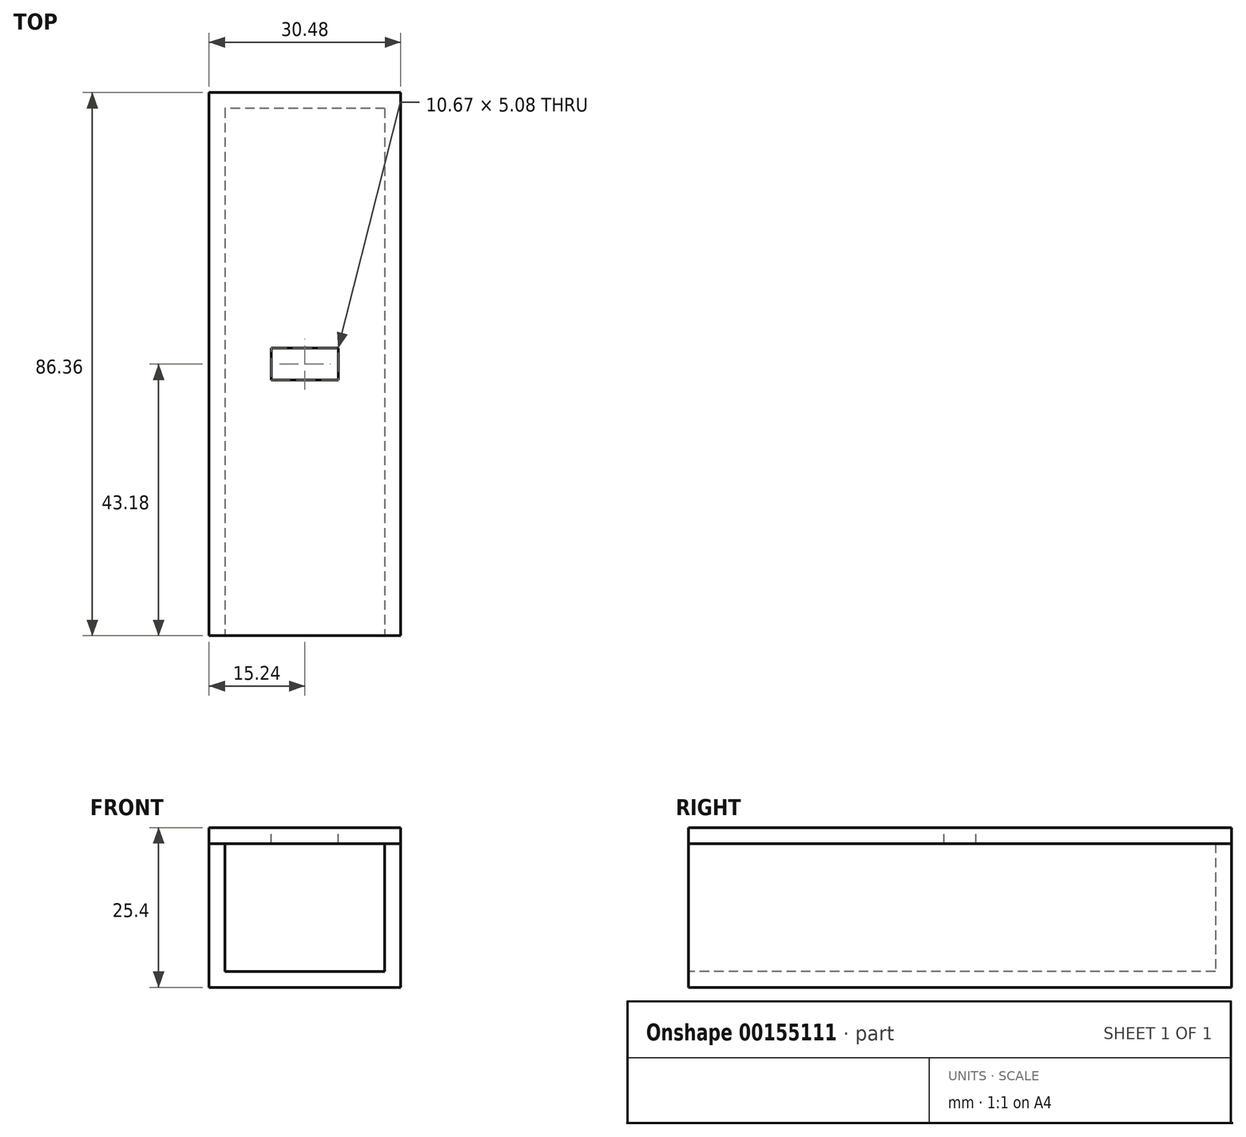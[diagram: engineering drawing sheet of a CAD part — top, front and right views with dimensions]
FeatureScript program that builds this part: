
annotation { "Feature Type Name" : "Feature", "Feature Type Description" : "" }
export const myFeature = defineFeature(function(context is Context, id is Id, definition is map)
    precondition{}
    {
        {
            var Q0;
            Q0=qCreatedBy(makeId("Top.planeOp"),FACE);
            var sketch = newSketch(context, id + "F0", { "sketchPlane" : qUnion([Q0])});
            skLineSegment(sketch, "E0.bottom", {"start": v(12.7, 40.64) * mm, "end": v(-12.7, 40.64) * mm});
            skLineSegment(sketch, "E0.top", {"start": v(12.7, -40.64) * mm, "end": v(-12.7, -40.64) * mm});
            skLineSegment(sketch, "E0.left", {"start": v(12.7, 40.64) * mm, "end": v(12.7, -40.64) * mm});
            skLineSegment(sketch, "E0.right", {"start": v(-12.7, 40.64) * mm, "end": v(-12.7, -40.64) * mm});
            skPoint(sketch, "E0.middle", {"position": v(0, 0) * mm});
            skLineSegment(sketch, "E1.bottom", {"start": v(15.24, 43.18) * mm, "end": v(-15.24, 43.18) * mm});
            skLineSegment(sketch, "E1.top", {"start": v(15.24, -43.18) * mm, "end": v(-15.24, -43.18) * mm});
            skLineSegment(sketch, "E1.left", {"start": v(15.24, 43.18) * mm, "end": v(15.24, -43.18) * mm});
            skLineSegment(sketch, "E1.right", {"start": v(-15.24, 43.18) * mm, "end": v(-15.24, -43.18) * mm});
            skLineSegment(sketch, "E2", {"start": v(-12.7, -40.64) * mm, "end": v(-12.7, -43.18) * mm});
            skLineSegment(sketch, "E3", {"start": v(-12.7, -43.18) * mm, "end": v(12.7, -43.18) * mm});
            skLineSegment(sketch, "E4", {"start": v(12.7, -43.18) * mm, "end": v(12.7, -40.64) * mm});
            skSolve(sketch);
        }
        {
            var Q0;
            Q0 = qSketchRegion(id + "F0", true);
            var Q1;
            Q1=makeQuery(id+"F0.imprint","IMPRINT",FACE,{"disambiguationData":[TD([[makeQuery(id+"F0.imprint","IMPRINT",EDGE,{"derivedFrom":sQuery(id+"F0.wireOp",EDGE,"E0.bottom")}),1.0]])]});
            extrude(context, id + "F1", {"entities" : qUnion([Q0, Q1]), "oppositeDirection" : true, "depth" : 2.54 * mm});
        }
        {
            var Q0;
            Q0=makeQuery(id+"F0.imprint","IMPRINT",FACE,{"disambiguationData":[TD([[makeQuery(id+"F0.imprint","IMPRINT",EDGE,{"derivedFrom":sQuery(id+"F0.wireOp",EDGE,"E0.bottom")}),-1.0]])]});
            extrude(context, id + "F2", {"entities" : qUnion([Q0]), "operationType" : NewBodyOperationType.ADD, "depth" : 20.32 * mm});
        }
        {
            var Q0;
            Q0=makeQuery(id+"F0.imprint","IMPRINT",FACE,{"disambiguationData":[TD([[makeQuery(id+"F0.imprint","IMPRINT",EDGE,{"derivedFrom":sQuery(id+"F0.wireOp",EDGE,"E0.bottom")}),1.0]])]});
            var Q1;
            Q1=makeQuery(id+"F0.imprint","IMPRINT",FACE,{"disambiguationData":[TD([[makeQuery(id+"F0.imprint","IMPRINT",EDGE,{"derivedFrom":sQuery(id+"F0.wireOp",EDGE,"E0.bottom")}),-1.0]])]});
            var Q2;
            Q2=makeQuery(id+"F0.imprint","IMPRINT",FACE,{"disambiguationData":[TD([[makeQuery(id+"F0.imprint","IMPRINT",EDGE,{"derivedFrom":sQuery(id+"F0.wireOp",EDGE,"E0.top")}),1.0]])]});
            extrude(context, id + "F3", {"entities" : qUnion([Q0, Q1, Q2]), "depth" : 22.86 * mm, "hasSecondDirection" : true, "secondDirectionOppositeDirection" : false, "secondDirectionDepth" : 20.32 * mm});
        }
        {
            var Q0;
            Q0=makeQuery(id+"F3.opExtrude","CAP_FACE",FACE,{"disambiguationData":[OSD([sQuery(id+"F0.wireOp",EDGE,"E1.bottom"),sQuery(id+"F0.wireOp",EDGE,"E1.top"),sQuery(id+"F0.wireOp",EDGE,"E1.left"),sQuery(id+"F0.wireOp",EDGE,"E1.right"),sQuery(id+"F0.wireOp",EDGE,"E3")])],"isStart":false});
            var sketch = newSketch(context, id + "F4", { "sketchPlane" : qUnion([Q0])});
            skLineSegment(sketch, "E5.bottom", {"start": v(5.33, 2.54) * mm, "end": v(-5.33, 2.54) * mm});
            skLineSegment(sketch, "E5.top", {"start": v(5.33, -2.54) * mm, "end": v(-5.33, -2.54) * mm});
            skLineSegment(sketch, "E5.left", {"start": v(5.33, 2.54) * mm, "end": v(5.33, -2.54) * mm});
            skLineSegment(sketch, "E5.right", {"start": v(-5.33, 2.54) * mm, "end": v(-5.33, -2.54) * mm});
            skPoint(sketch, "E5.middle", {"position": v(0, 0) * mm});
            skSolve(sketch);
        }
        {
            var Q0;
            Q0 = qSketchRegion(id + "F4", true);
            extrude(context, id + "F5", {"entities" : qUnion([Q0]), "operationType" : NewBodyOperationType.REMOVE, "oppositeDirection" : true, "depth" : 5.08 * mm});
        }
    });
